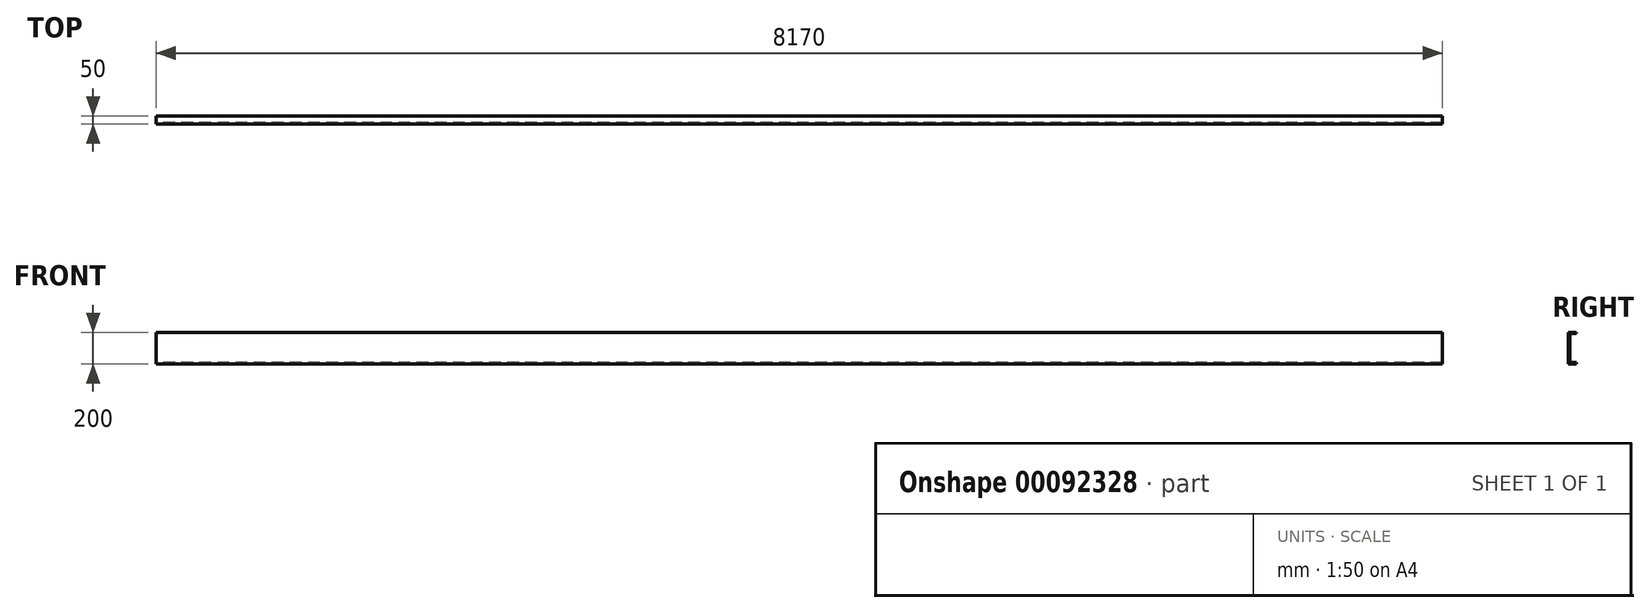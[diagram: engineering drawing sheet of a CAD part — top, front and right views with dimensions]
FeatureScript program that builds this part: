
annotation { "Feature Type Name" : "Feature", "Feature Type Description" : "" }
export const myFeature = defineFeature(function(context is Context, id is Id, definition is map)
    precondition{}
    {
        {
            var Q0;
            Q0=qCreatedBy(makeId("Right.planeOp"),FACE);
            var sketch = newSketch(context, id + "F0", { "sketchPlane" : qUnion([Q0])});
            skLineSegment(sketch, "E0", {"start": v(0, 0) * mm, "end": v(-50, 0) * mm});
            skLineSegment(sketch, "E1", {"start": v(-50, 0) * mm, "end": v(-50, 200) * mm});
            skLineSegment(sketch, "E2", {"start": v(-50, 200) * mm, "end": v(0, 200) * mm});
            skLineSegment(sketch, "E3", {"start": v(0, 200) * mm, "end": v(0, 192) * mm});
            skLineSegment(sketch, "E4", {"start": v(0, 192) * mm, "end": v(-42, 192) * mm});
            skLineSegment(sketch, "E5", {"start": v(-42, 192) * mm, "end": v(-42, 8) * mm});
            skLineSegment(sketch, "E6", {"start": v(-42, 8) * mm, "end": v(0, 8) * mm});
            skLineSegment(sketch, "E7", {"start": v(0, 8) * mm, "end": v(0, 0) * mm});
            skSolve(sketch);
        }
        {
            var Q0;
            Q0 = qSketchRegion(id + "F0", true);
            extrude(context, id + "F1", {"entities" : qUnion([Q0]), "depth" : 8170 * mm});
        }
    });
